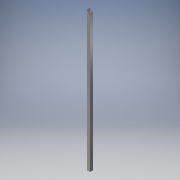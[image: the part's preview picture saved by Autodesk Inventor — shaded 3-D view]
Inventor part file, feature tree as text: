
AUTODESK INVENTOR PART (.ipt)
format: ipt  version: 2019 (Build 230136000, 136)  size: 121,856 bytes
history: native  units: mm
features: other x3, sketch x2
ambient origin geometry x8: Origin, YZ Plane, XZ Plane, XY Plane, X Axis, Y Axis, Z Axis, Center Point
bodies: Solid1 (feature_tree)
feature tree (5):
  other  "1500mm_box_section.ipt"
  other  "Solid1::1500mm_box_section.ipt"
  other  "TaggingFeature1"
  sketch  "Sketch1"  dims[d0=10.0mm]
  sketch  "Sketch2"
